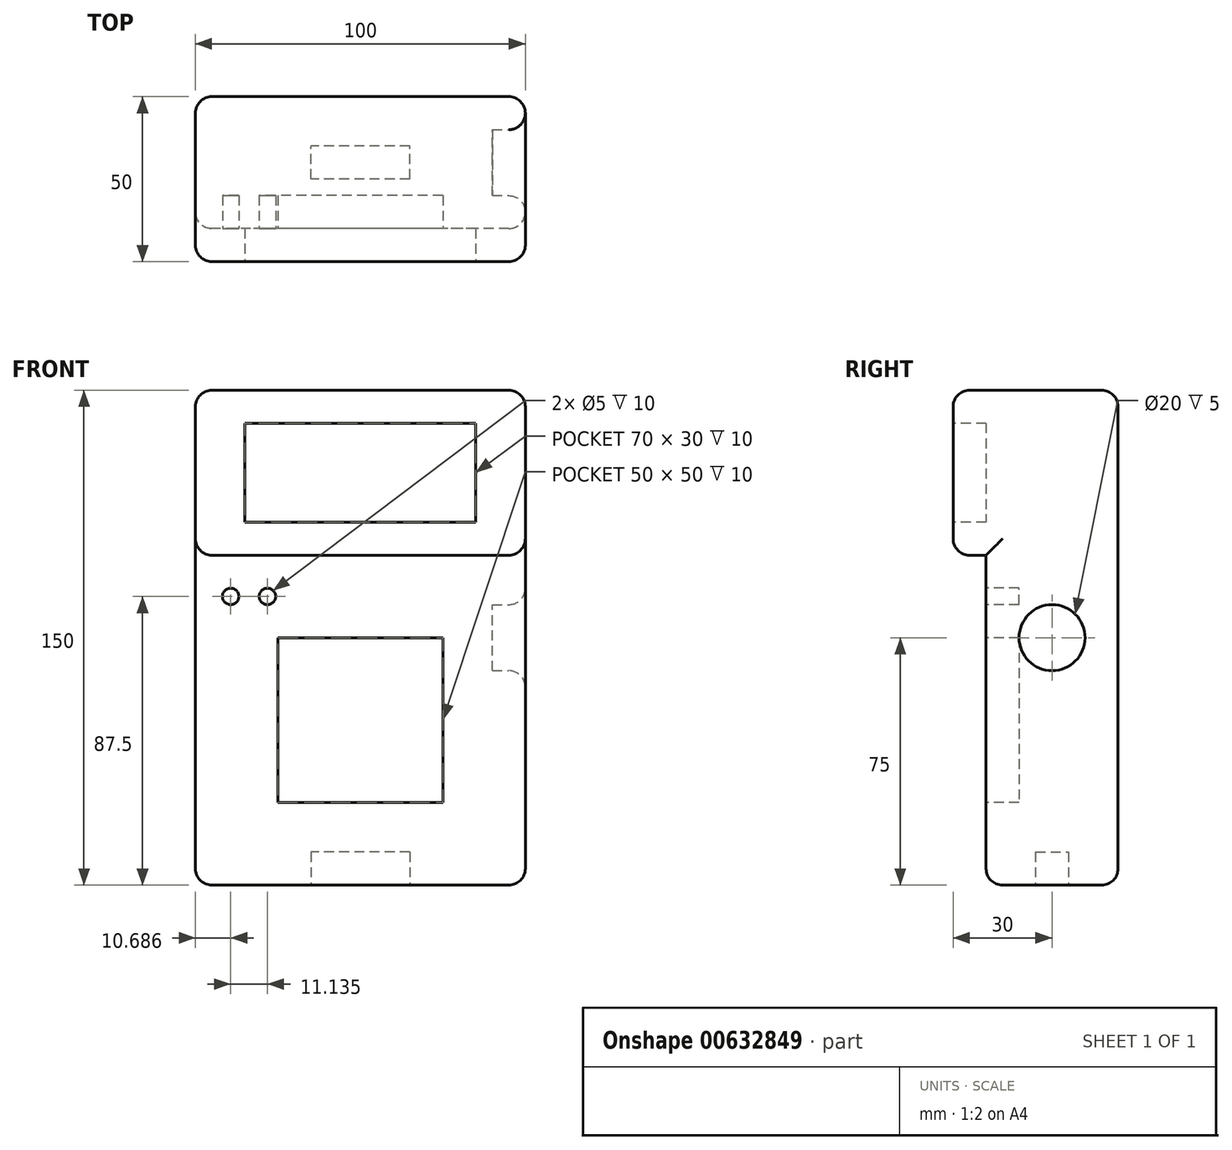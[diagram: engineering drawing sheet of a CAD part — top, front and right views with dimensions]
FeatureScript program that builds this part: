
annotation { "Feature Type Name" : "Feature", "Feature Type Description" : "" }
export const myFeature = defineFeature(function(context is Context, id is Id, definition is map)
    precondition{}
    {
        {
            var Q0;
            Q0=qCreatedBy(makeId("Front.planeOp"),FACE);
            var sketch = newSketch(context, id + "F0", { "sketchPlane" : qUnion([Q0])});
            skLineSegment(sketch, "E0.bottom", {"start": v(50, 75) * mm, "end": v(-50, 75) * mm});
            skLineSegment(sketch, "E0.top", {"start": v(50, -75) * mm, "end": v(-50, -75) * mm});
            skLineSegment(sketch, "E0.left", {"start": v(50, 75) * mm, "end": v(50, -75) * mm});
            skLineSegment(sketch, "E0.right", {"start": v(-50, 75) * mm, "end": v(-50, -75) * mm});
            skPoint(sketch, "E0.middle", {"position": v(0, 0) * mm});
            skLineSegment(sketch, "E1", {"start": v(-50, 25) * mm, "end": v(50, 25) * mm, "construction": true});
            skLineSegment(sketch, "E2", {"start": v(-50, 25) * mm, "end": v(50, 25) * mm});
            skSolve(sketch);
        }
        {
            var Q0;
            Q0=makeQuery(id+"F0.imprint","IMPRINT",FACE,{"disambiguationData":[TD([[makeQuery(id+"F0.imprint","IMPRINT",EDGE,{"derivedFrom":sQuery(id+"F0.wireOp",EDGE,"E0.bottom")}),1.0]])]});
            extrude(context, id + "F1", {"entities" : qUnion([Q0]), "depth" : 50 * mm, "offsetDistance" : 25.4 * mm});
        }
        {
            var Q0;
            Q0=makeQuery(id+"F1.opExtrude","SWEPT_FACE",FACE,{"disambiguationData":[OSD([sQuery(id+"F0.wireOp",EDGE,"E0.left")])]});
            var sketch = newSketch(context, id + "F2", { "sketchPlane" : qUnion([Q0])});
            skLineSegment(sketch, "E3", {"start": v(-50, 50) * mm, "end": v(0, 0) * mm, "construction": true});
            skCircle(sketch, "E4", {"center": v(-25, 25) * mm, "radius": 10 * mm});
            skSolve(sketch);
        }
        {
            var Q0;
            Q0=makeQuery(id+"F2.imprint","IMPRINT",FACE,{"disambiguationData":[TD([[makeQuery(id+"F2.imprint","IMPRINT",EDGE,{"derivedFrom":sQuery(id+"F2.wireOp",EDGE,"E4")}),1.0]])]});
            extrude(context, id + "F3", {"entities" : qUnion([Q0]), "operationType" : NewBodyOperationType.REMOVE, "oppositeDirection" : true, "depth" : 10 * mm, "offsetDistance" : 25.4 * mm});
        }
        {
            var Q0;
            Q0 = qSketchRegion(id + "F0", true);
            extrude(context, id + "F4", {"entities" : qUnion([Q0]), "operationType" : NewBodyOperationType.ADD, "depth" : 40 * mm, "offsetDistance" : 25.4 * mm});
        }
        {
            var Q0;
            {var subQ0=sQuery(id+"F0.wireOp",EDGE,"E0.left");Q0=makeQuery(id+"F4.boolean.opBoolean","MERGE",FACE,{"derivedFrom":[makeQuery(id+"F1.opExtrude","SWEPT_FACE",FACE,{"disambiguationData":[OSD([subQ0])]}),makeQuery(id+"F4.opExtrude","SWEPT_FACE",FACE,{"disambiguationData":[OSD([subQ0])]})]});}
            var sketch = newSketch(context, id + "F5", { "sketchPlane" : qUnion([Q0])});
            skLineSegment(sketch, "E5", {"start": v(-40, 0) * mm, "end": v(0, 0) * mm, "construction": true});
            skCircle(sketch, "E6", {"center": v(-20, 0) * mm, "radius": 10 * mm});
            skSolve(sketch);
        }
        {
            var Q0;
            Q0=makeQuery(id+"F5.imprint","IMPRINT",FACE,{"disambiguationData":[TD([[makeQuery(id+"F5.imprint","IMPRINT",EDGE,{"derivedFrom":sQuery(id+"F5.wireOp",EDGE,"E6")}),1.0]])]});
            extrude(context, id + "F6", {"entities" : qUnion([Q0]), "operationType" : NewBodyOperationType.REMOVE, "oppositeDirection" : true, "depth" : 10 * mm, "offsetDistance" : 25.4 * mm});
        }
        {
            var Q0;
            Q0=makeQuery(id+"F1.opExtrude","CAP_FACE",FACE,{"disambiguationData":[OSD([sQuery(id+"F0.wireOp",EDGE,"E0.bottom"),sQuery(id+"F0.wireOp",EDGE,"E0.left"),sQuery(id+"F0.wireOp",EDGE,"E0.right"),sQuery(id+"F0.wireOp",EDGE,"E2")])],"isStart":false});
            var sketch = newSketch(context, id + "F7", { "sketchPlane" : qUnion([Q0])});
            skLineSegment(sketch, "E7", {"start": v(50, 50) * mm, "end": v(-50, 50) * mm, "construction": true});
            skLineSegment(sketch, "E8.bottom", {"start": v(35, 65) * mm, "end": v(-35, 65) * mm});
            skLineSegment(sketch, "E8.top", {"start": v(35, 35) * mm, "end": v(-35, 35) * mm});
            skLineSegment(sketch, "E8.left", {"start": v(35, 65) * mm, "end": v(35, 35) * mm});
            skLineSegment(sketch, "E8.right", {"start": v(-35, 65) * mm, "end": v(-35, 35) * mm});
            skPoint(sketch, "E8.middle", {"position": v(0, 50) * mm});
            skSolve(sketch);
        }
        {
            var Q0;
            Q0=makeQuery(id+"F7.imprint","IMPRINT",FACE,{"disambiguationData":[TD([[makeQuery(id+"F7.imprint","IMPRINT",EDGE,{"derivedFrom":sQuery(id+"F7.wireOp",EDGE,"E8.bottom")}),1.0]])]});
            extrude(context, id + "F8", {"entities" : qUnion([Q0]), "operationType" : NewBodyOperationType.REMOVE, "oppositeDirection" : true, "depth" : 10 * mm, "offsetDistance" : 25.4 * mm});
        }
        {
            var Q0;
            Q0=makeQuery(id+"F4.opExtrude","SWEPT_FACE",FACE,{"disambiguationData":[OSD([sQuery(id+"F0.wireOp",EDGE,"E0.top")])]});
            var sketch = newSketch(context, id + "F9", { "sketchPlane" : qUnion([Q0])});
            skLineSegment(sketch, "E9", {"start": v(50, 20) * mm, "end": v(-50, 20) * mm, "construction": true});
            skLineSegment(sketch, "E10.bottom", {"start": v(15, 25) * mm, "end": v(-15, 25) * mm});
            skLineSegment(sketch, "E10.top", {"start": v(15, 15) * mm, "end": v(-15, 15) * mm});
            skLineSegment(sketch, "E10.left", {"start": v(15, 25) * mm, "end": v(15, 15) * mm});
            skLineSegment(sketch, "E10.right", {"start": v(-15, 25) * mm, "end": v(-15, 15) * mm});
            skPoint(sketch, "E10.middle", {"position": v(0, 20) * mm});
            skSolve(sketch);
        }
        {
            var Q0;
            Q0=makeQuery(id+"F9.imprint","IMPRINT",FACE,{"disambiguationData":[TD([[makeQuery(id+"F9.imprint","IMPRINT",EDGE,{"derivedFrom":sQuery(id+"F9.wireOp",EDGE,"E10.bottom")}),1.0]])]});
            extrude(context, id + "F10", {"entities" : qUnion([Q0]), "operationType" : NewBodyOperationType.REMOVE, "oppositeDirection" : true, "depth" : 10 * mm, "offsetDistance" : 25.4 * mm});
        }
        {
            var Q0;
            Q0=makeQuery(id+"F4.opExtrude","CAP_FACE",FACE,{"disambiguationData":[OSD([sQuery(id+"F0.wireOp",EDGE,"E0.bottom"),sQuery(id+"F0.wireOp",EDGE,"E0.top"),sQuery(id+"F0.wireOp",EDGE,"E0.left"),sQuery(id+"F0.wireOp",EDGE,"E0.right")])],"isStart":false});
            var sketch = newSketch(context, id + "F11", { "sketchPlane" : qUnion([Q0])});
            skLineSegment(sketch, "E11", {"start": v(-50, -25) * mm, "end": v(50, -25) * mm, "construction": true});
            skLineSegment(sketch, "E12.bottom", {"start": v(25, 0) * mm, "end": v(-25, 0) * mm});
            skLineSegment(sketch, "E12.top", {"start": v(25, -50) * mm, "end": v(-25, -50) * mm});
            skLineSegment(sketch, "E12.left", {"start": v(25, 0) * mm, "end": v(25, -50) * mm});
            skLineSegment(sketch, "E12.right", {"start": v(-25, 0) * mm, "end": v(-25, -50) * mm});
            skPoint(sketch, "E12.middle", {"position": v(0, -25) * mm});
            skSolve(sketch);
        }
        {
            var Q0;
            Q0=makeQuery(id+"F11.imprint","IMPRINT",FACE,{"disambiguationData":[TD([[makeQuery(id+"F11.imprint","IMPRINT",EDGE,{"derivedFrom":sQuery(id+"F11.wireOp",EDGE,"E12.bottom")}),1.0]])]});
            extrude(context, id + "F12", {"entities" : qUnion([Q0]), "operationType" : NewBodyOperationType.REMOVE, "oppositeDirection" : true, "depth" : 10 * mm, "offsetDistance" : 25.4 * mm});
        }
        {
            var Q0;
            Q0=makeQuery(id+"F1.opExtrude","CAP_EDGE",EDGE,{"disambiguationData":[OSD([sQuery(id+"F0.wireOp",EDGE,"E0.bottom")])],"isStart":false});
            var Q1;
            Q1=makeQuery(id+"F1.opExtrude","CAP_EDGE",EDGE,{"disambiguationData":[OSD([sQuery(id+"F0.wireOp",EDGE,"E0.right")])],"isStart":false});
            var Q2;
            Q2=makeQuery(id+"F1.opExtrude","CAP_EDGE",EDGE,{"disambiguationData":[OSD([sQuery(id+"F0.wireOp",EDGE,"E0.left")])],"isStart":false});
            var Q3;
            Q3=makeQuery(id+"F1.opExtrude","CAP_EDGE",EDGE,{"disambiguationData":[OSD([sQuery(id+"F0.wireOp",EDGE,"E2")])],"isStart":false});
            var Q4;
            Q4=makeQuery(id+"F4.opExtrude","CAP_EDGE",EDGE,{"disambiguationData":[OSD([sQuery(id+"F0.wireOp",EDGE,"E0.right")])],"isStart":false});
            var Q5;
            Q5=makeQuery(id+"F4.opExtrude","CAP_EDGE",EDGE,{"disambiguationData":[OSD([sQuery(id+"F0.wireOp",EDGE,"E0.left")])],"isStart":false});
            var Q6;
            Q6=makeQuery(id+"F4.opExtrude","CAP_EDGE",EDGE,{"disambiguationData":[OSD([sQuery(id+"F0.wireOp",EDGE,"E0.top")])],"isStart":false});
            var Q7;
            Q7=makeQuery(id+"F1.opExtrude","CAP_EDGE",EDGE,{"disambiguationData":[OSD([sQuery(id+"F0.wireOp",EDGE,"E0.bottom")])],"isStart":true});
            var Q8;
            {var subQ0=sQuery(id+"F0.wireOp",EDGE,"E0.right");Q8=makeQuery(id+"F4.boolean.opBoolean","MERGE",EDGE,{"derivedFrom":[makeQuery(id+"F1.opExtrude","CAP_EDGE",EDGE,{"disambiguationData":[OSD([subQ0])],"isStart":true}),makeQuery(id+"F4.opExtrude","CAP_EDGE",EDGE,{"disambiguationData":[OSD([subQ0])],"isStart":true})]});}
            var Q9;
            Q9=makeQuery(id+"F1.opExtrude","SWEPT_EDGE",EDGE,{"disambiguationData":[OSD([sQuery(id+"F0.wireOp",EDGE,"E0.bottom"),sQuery(id+"F0.wireOp",EDGE,"E0.left")])]});
            var Q10;
            Q10=makeQuery(id+"F1.opExtrude","SWEPT_EDGE",EDGE,{"disambiguationData":[OSD([sQuery(id+"F0.wireOp",EDGE,"E0.bottom"),sQuery(id+"F0.wireOp",EDGE,"E0.right")])]});
            var Q11;
            {var subQ0=sQuery(id+"F0.wireOp",EDGE,"E0.left");Q11=makeQuery(id+"F4.boolean.opBoolean","MERGE",FACE,{"derivedFrom":[makeQuery(id+"F1.opExtrude","SWEPT_FACE",FACE,{"disambiguationData":[OSD([subQ0])]}),makeQuery(id+"F4.opExtrude","SWEPT_FACE",FACE,{"disambiguationData":[OSD([subQ0])]})]});}
            var Q12;
            Q12=makeQuery(id+"F4.opExtrude","SWEPT_EDGE",EDGE,{"disambiguationData":[OSD([sQuery(id+"F0.wireOp",EDGE,"E0.top"),sQuery(id+"F0.wireOp",EDGE,"E0.left")])]});
            var Q13;
            Q13=makeQuery(id+"F4.opExtrude","CAP_EDGE",EDGE,{"disambiguationData":[OSD([sQuery(id+"F0.wireOp",EDGE,"E0.top")])],"isStart":true});
            var Q14;
            Q14=makeQuery(id+"F4.opExtrude","SWEPT_EDGE",EDGE,{"disambiguationData":[OSD([sQuery(id+"F0.wireOp",EDGE,"E0.top"),sQuery(id+"F0.wireOp",EDGE,"E0.right")])]});
            var Q15;
            {var subQ0=sQuery(id+"F0.wireOp",EDGE,"E2");var subQ1=sQuery(id+"F0.wireOp",EDGE,"E0.left");Q15=makeQuery(id+"F3.boolean.opBoolean","SPLIT",EDGE,{"disambiguationData":[TD([makeQuery(id+"F1.opExtrude","CAP_FACE",FACE,{"disambiguationData":[OSD([sQuery(id+"F0.wireOp",EDGE,"E0.bottom"),subQ1,sQuery(id+"F0.wireOp",EDGE,"E0.right"),subQ0])],"isStart":false})])],"derivedFrom":makeQuery(id+"F1.opExtrude","SWEPT_EDGE",EDGE,{"disambiguationData":[OSD([subQ1,subQ0])]})});}
            var Q16;
            Q16=makeQuery(id+"F1.opExtrude","SWEPT_EDGE",EDGE,{"disambiguationData":[OSD([sQuery(id+"F0.wireOp",EDGE,"E0.right"),sQuery(id+"F0.wireOp",EDGE,"E2")])]});
            fillet(context, id + "F13", {"entities" : qUnion([Q0, Q1, Q2, Q3, Q4, Q5, Q6, Q7, Q8, Q9, Q10, Q11, Q12, Q13, Q14, Q15, Q16]), "radius" : 5 * mm, "tangentPropagation" : true, "allowEdgeOverflow" : false});
        }
        {
            var Q0;
            Q0=makeQuery(id+"F4.opExtrude","CAP_FACE",FACE,{"disambiguationData":[OSD([sQuery(id+"F0.wireOp",EDGE,"E0.bottom"),sQuery(id+"F0.wireOp",EDGE,"E0.top"),sQuery(id+"F0.wireOp",EDGE,"E0.left"),sQuery(id+"F0.wireOp",EDGE,"E0.right")])],"isStart":false});
            var sketch = newSketch(context, id + "F14", { "sketchPlane" : qUnion([Q0])});
            skCircle(sketch, "E13", {"center": v(-39.31, 12.5) * mm, "radius": 2.5 * mm});
            skCircle(sketch, "E14", {"center": v(-28.18, 12.5) * mm, "radius": 2.5 * mm});
            skSolve(sketch);
        }
        {
            var Q0;
            Q0=makeQuery(id+"F14.imprint","IMPRINT",FACE,{"disambiguationData":[TD([[makeQuery(id+"F14.imprint","IMPRINT",EDGE,{"derivedFrom":sQuery(id+"F14.wireOp",EDGE,"E13")}),1.0]])]});
            var Q1;
            Q1=makeQuery(id+"F14.imprint","IMPRINT",FACE,{"disambiguationData":[TD([[makeQuery(id+"F14.imprint","IMPRINT",EDGE,{"derivedFrom":sQuery(id+"F14.wireOp",EDGE,"E14")}),1.0]])]});
            extrude(context, id + "F15", {"entities" : qUnion([Q0, Q1]), "operationType" : NewBodyOperationType.REMOVE, "oppositeDirection" : true, "depth" : 10 * mm, "offsetDistance" : 25.4 * mm});
        }
    });
